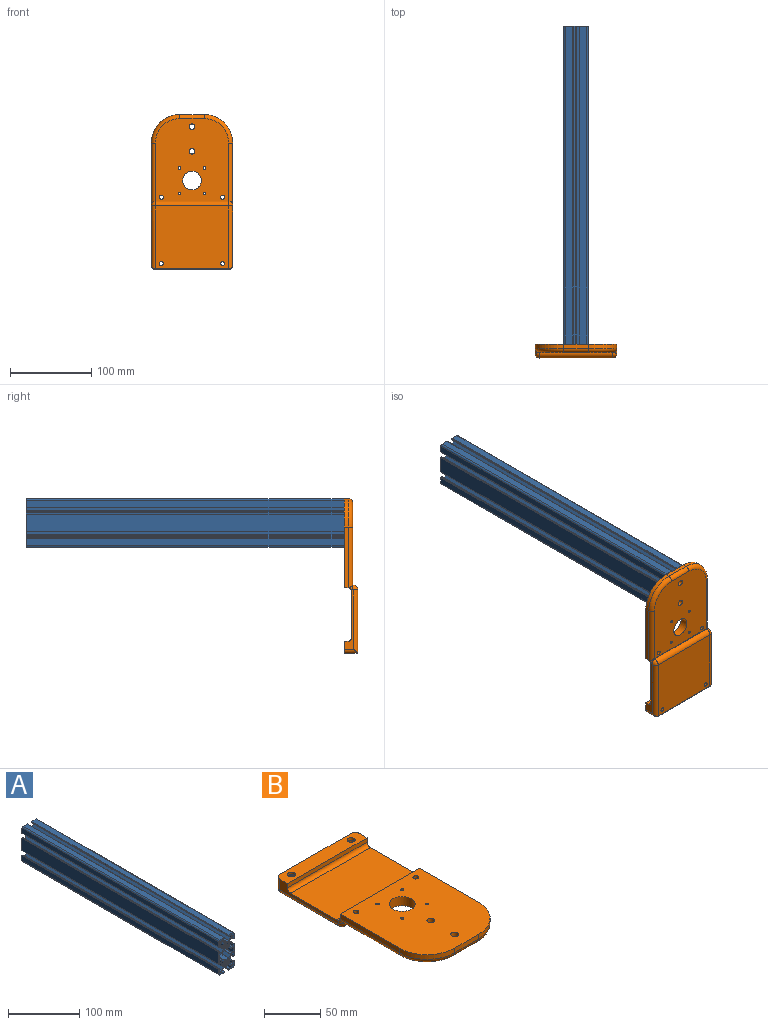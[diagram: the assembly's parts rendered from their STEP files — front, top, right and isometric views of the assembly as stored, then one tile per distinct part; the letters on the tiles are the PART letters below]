
ASSEMBLY  parts=2 mates=1
PART A: 312 faces, bbox 30x391x60 mm
  f0: cylinder r=0.4mm len=391mm, axis (0,1,0), area 245.7mm2, adj f1,f133,f310,f311
  f1: plane 391x8.6mm, normal (-1,0,0), area 3362.6mm2, adj f0,f2,f310,f311
  f2: cylinder r=2mm len=391mm, axis (0,1,0), area 1228.4mm2, adj f1,f3,f310,f311
  f3: plane 391x8.6mm, normal (0,0,-1), area 3362.6mm2, adj f2,f4,f310,f311
  f4: cylinder r=0.4mm len=391mm, axis (0,1,0), area 245.7mm2, adj f3,f5,f310,f311
  f5: plane 391x1.2mm, normal (1,0,0), area 469.2mm2, adj f4,f6,f310,f311
  f6: cylinder r=0.4mm len=391mm, axis (0,1,0), area 245.7mm2, adj f5,f7,f310,f311
  f7: plane 391x3.85mm, normal (0,0,1), area 1505.4mm2, adj f6,f8,f310,f311
  f8: plane 391x3.34mm, normal (1,0,0), area 1304.3mm2, adj f7,f9,f310,f311
  f9: plane 391x3.66mm, normal (0.71,0,-0.71), area 2026.2mm2, adj f8,f10,f310,f311
  f10: plane 391x3.93mm, normal (0,0,-1), area 1537.5mm2, adj f9,f11,f310,f311
  f11: cylinder r=0.5mm len=391mm, axis (0,1,0), area 102.4mm2, adj f10,f12,f310,f311
  f12: plane 391x0.4mm, normal (0.5,0,-0.87), area 182.2mm2, adj f11,f13,f310,f311
  f13: plane 391x0.4mm, normal (-0.5,0,-0.87), area 182.2mm2, adj f12,f14,f310,f311
  f14: cylinder r=0.5mm len=391mm, axis (0,1,0), area 204.7mm2, adj f13,f15,f310,f311
  f15: plane 391x0.32mm, normal (0.5,0,-0.87), area 142.4mm2, adj f14,f16,f310,f311
  f16: plane 391x1.28mm, normal (-0.19,0,-0.98), area 510.3mm2, adj f15,f17,f310,f311
  f17: plane 391x2.09mm, normal (0,0,-1), area 815.5mm2, adj f16,f18,f310,f311
  f18: plane 391x3.66mm, normal (-0.71,0,-0.71), area 2026.2mm2, adj f17,f19,f310,f311
  f19: plane 391x3.34mm, normal (-1,0,0), area 1304.3mm2, adj f18,f20,f310,f311
  f20: plane 391x3.85mm, normal (0,0,1), area 1505.4mm2, adj f19,f21,f310,f311
  f21: cylinder r=0.4mm len=391mm, axis (0,1,0), area 245.7mm2, adj f20,f22,f310,f311
  f22: plane 391x1.2mm, normal (-1,0,0), area 469.2mm2, adj f21,f23,f310,f311
  f23: cylinder r=0.4mm len=391mm, axis (0,1,0), area 245.7mm2, adj f22,f24,f310,f311
  f24: plane 391x8.6mm, normal (0,0,-1), area 3362.6mm2, adj f23,f25,f310,f311
  f25: cylinder r=2mm len=391mm, axis (0,1,0), area 1228.4mm2, adj f24,f26,f310,f311
  f26: plane 391x8.6mm, normal (1,0,0), area 3362.6mm2, adj f25,f27,f310,f311
  f27: cylinder r=0.4mm len=391mm, axis (0,1,0), area 245.7mm2, adj f26,f28,f310,f311
  f28: plane 391x1.2mm, normal (0,0,1), area 469.2mm2, adj f27,f29,f310,f311
  f29: cylinder r=0.4mm len=391mm, axis (0,1,0), area 245.7mm2, adj f28,f30,f310,f311
  f30: plane 391x3.85mm, normal (-1,0,0), area 1505.3mm2, adj f29,f31,f310,f311
  f31: plane 391x3.34mm, normal (0,0,1), area 1304.3mm2, adj f30,f32,f310,f311
  f32: plane 391x3.66mm, normal (0.71,0,0.71), area 2026.2mm2, adj f31,f33,f310,f311
  f33: plane 391x3.93mm, normal (1,0,0), area 1537.5mm2, adj f32,f34,f310,f311
  f34: cylinder r=0.5mm len=391mm, axis (0,1,0), area 102.4mm2, adj f33,f35,f310,f311
  f35: plane 391x0.4mm, normal (0.87,0,0.5), area 182.2mm2, adj f34,f36,f310,f311
  f36: plane 391x0.4mm, normal (0.87,0,-0.5), area 182.2mm2, adj f35,f37,f310,f311
  f37: cylinder r=0.5mm len=391mm, axis (0,1,0), area 204.7mm2, adj f36,f38,f310,f311
  f38: plane 391x0.32mm, normal (0.87,0,0.5), area 142.4mm2, adj f37,f39,f310,f311
  f39: plane 391x1.28mm, normal (0.98,0,-0.19), area 510.3mm2, adj f38,f40,f310,f311
  f40: plane 391x2.09mm, normal (1,0,0), area 815.5mm2, adj f39,f41,f310,f311
  f41: plane 391x3.66mm, normal (0.71,0,-0.71), area 2026.2mm2, adj f40,f42,f310,f311
  f42: plane 391x3.34mm, normal (0,0,-1), area 1304.3mm2, adj f41,f43,f310,f311
  f43: plane 391x3.85mm, normal (-1,0,0), area 1505.4mm2, adj f42,f44,f310,f311
  f44: cylinder r=0.4mm len=391mm, axis (0,1,0), area 245.7mm2, adj f43,f45,f310,f311
  f45: plane 391x1.2mm, normal (0,0,-1), area 469.2mm2, adj f44,f46,f310,f311
  f46: cylinder r=0.4mm len=391mm, axis (0,1,0), area 245.7mm2, adj f45,f47,f310,f311
  f47: plane 391x21.2mm, normal (1,0,0), area 8289.2mm2, adj f46,f48,f310,f311
  f48: cylinder r=0.4mm len=391mm, axis (0,1,0), area 245.7mm2, adj f47,f49,f310,f311
  f49: plane 391x1.2mm, normal (0,0,1), area 469.2mm2, adj f48,f50,f310,f311
  f50: cylinder r=0.4mm len=391mm, axis (0,1,0), area 245.7mm2, adj f49,f51,f310,f311
  f51: plane 391x3.85mm, normal (-1,0,0), area 1505.4mm2, adj f50,f52,f310,f311
  f52: plane 391x3.34mm, normal (0,0,1), area 1304.3mm2, adj f51,f53,f310,f311
  f53: plane 391x3.66mm, normal (0.71,0,0.71), area 2026.2mm2, adj f52,f54,f310,f311
  f54: plane 391x3.93mm, normal (1,0,0), area 1537.5mm2, adj f53,f55,f310,f311
  f55: cylinder r=0.5mm len=391mm, axis (0,1,0), area 102.4mm2, adj f54,f56,f310,f311
  f56: plane 391x0.4mm, normal (0.87,0,0.5), area 182.2mm2, adj f55,f57,f310,f311
  f57: plane 391x0.4mm, normal (0.87,0,-0.5), area 182.2mm2, adj f56,f58,f310,f311
  f58: cylinder r=0.5mm len=391mm, axis (0,1,0), area 204.7mm2, adj f57,f59,f310,f311
  f59: plane 391x0.32mm, normal (0.87,0,0.5), area 142.4mm2, adj f58,f60,f310,f311
  f60: plane 391x1.28mm, normal (0.98,0,-0.19), area 510.3mm2, adj f59,f61,f310,f311
  f61: plane 391x2.09mm, normal (1,0,0), area 815.5mm2, adj f60,f62,f310,f311
  f62: plane 391x3.66mm, normal (0.71,0,-0.71), area 2026.2mm2, adj f61,f63,f310,f311
  f63: plane 391x3.34mm, normal (0,0,-1), area 1304.3mm2, adj f62,f64,f310,f311
  f64: plane 391x3.85mm, normal (-1,0,0), area 1505.3mm2, adj f63,f65,f310,f311
  f65: cylinder r=0.4mm len=391mm, axis (0,1,0), area 245.7mm2, adj f64,f66,f310,f311
  f66: plane 391x1.2mm, normal (0,0,-1), area 469.2mm2, adj f65,f67,f310,f311
  f67: cylinder r=0.4mm len=391mm, axis (0,1,0), area 245.7mm2, adj f66,f68,f310,f311
  f68: plane 391x8.6mm, normal (1,0,0), area 3362.6mm2, adj f67,f69,f310,f311
  f69: cylinder r=2mm len=391mm, axis (0,1,0), area 1228.4mm2, adj f68,f70,f310,f311
  f70: plane 391x8.6mm, normal (0,0,1), area 3362.6mm2, adj f69,f71,f310,f311
  f71: cylinder r=0.4mm len=391mm, axis (0,1,0), area 245.7mm2, adj f70,f72,f310,f311
  f72: plane 391x1.2mm, normal (-1,0,0), area 469.2mm2, adj f71,f73,f310,f311
  f73: cylinder r=0.4mm len=391mm, axis (0,1,0), area 245.7mm2, adj f72,f74,f310,f311
  f74: plane 391x3.85mm, normal (0,0,-1), area 1505.4mm2, adj f73,f75,f310,f311
  f75: plane 391x3.34mm, normal (-1,0,0), area 1304.3mm2, adj f74,f76,f310,f311
  f76: plane 391x3.66mm, normal (-0.71,0,0.71), area 2026.2mm2, adj f75,f77,f310,f311
  f77: plane 391x3.93mm, normal (0,0,1), area 1537.5mm2, adj f76,f78,f310,f311
  f78: cylinder r=0.5mm len=391mm, axis (0,1,0), area 102.4mm2, adj f77,f79,f310,f311
  f79: plane 391x0.4mm, normal (-0.5,0,0.87), area 182.2mm2, adj f78,f80,f310,f311
  f80: plane 391x0.4mm, normal (0.5,0,0.87), area 182.2mm2, adj f79,f81,f310,f311
  f81: cylinder r=0.5mm len=391mm, axis (0,1,0), area 204.7mm2, adj f80,f82,f310,f311
  f82: plane 391x0.32mm, normal (-0.5,0,0.87), area 142.4mm2, adj f81,f83,f310,f311
  f83: plane 391x1.28mm, normal (0.19,0,0.98), area 510.3mm2, adj f82,f84,f310,f311
  f84: plane 391x2.09mm, normal (0,0,1), area 815.5mm2, adj f83,f85,f310,f311
  f85: plane 391x3.66mm, normal (0.71,0,0.71), area 2026.2mm2, adj f84,f86,f310,f311
  f86: plane 391x3.34mm, normal (1,0,0), area 1304.3mm2, adj f85,f87,f310,f311
  f87: plane 391x3.85mm, normal (0,0,-1), area 1505.4mm2, adj f86,f88,f310,f311
  f88: cylinder r=0.4mm len=391mm, axis (0,1,0), area 245.7mm2, adj f87,f89,f310,f311
  f89: plane 391x1.2mm, normal (1,0,0), area 469.2mm2, adj f88,f90,f310,f311
  f90: cylinder r=0.4mm len=391mm, axis (0,1,0), area 245.7mm2, adj f89,f91,f310,f311
  f91: plane 391x8.6mm, normal (0,0,1), area 3362.6mm2, adj f90,f92,f310,f311
  f92: cylinder r=2mm len=391mm, axis (0,1,0), area 1228.4mm2, adj f91,f93,f310,f311
  f93: plane 391x8.6mm, normal (-1,0,0), area 3362.6mm2, adj f92,f94,f310,f311
  f94: cylinder r=0.4mm len=391mm, axis (0,1,0), area 245.7mm2, adj f93,f95,f310,f311
  f95: plane 391x1.2mm, normal (0,0,-1), area 469.2mm2, adj f94,f96,f310,f311
  f96: cylinder r=0.4mm len=391mm, axis (0,1,0), area 245.7mm2, adj f95,f97,f310,f311
  f97: plane 391x3.85mm, normal (1,0,0), area 1505.3mm2, adj f96,f98,f310,f311
  f98: plane 391x3.34mm, normal (0,0,-1), area 1304.3mm2, adj f97,f99,f310,f311
  f99: plane 391x3.66mm, normal (-0.71,0,-0.71), area 2026.2mm2, adj f98,f100,f310,f311
  f100: plane 391x3.93mm, normal (-1,0,0), area 1537.5mm2, adj f99,f101,f310,f311
  f101: cylinder r=0.5mm len=391mm, axis (0,1,0), area 102.4mm2, adj f100,f102,f310,f311
  f102: plane 391x0.4mm, normal (-0.87,0,-0.5), area 182.2mm2, adj f101,f103,f310,f311
  f103: plane 391x0.4mm, normal (-0.87,0,0.5), area 182.2mm2, adj f102,f104,f310,f311
  f104: cylinder r=0.5mm len=391mm, axis (0,1,0), area 204.7mm2, adj f103,f105,f310,f311
  f105: plane 391x0.32mm, normal (-0.87,0,-0.5), area 142.4mm2, adj f104,f106,f310,f311
  f106: plane 391x1.28mm, normal (-0.98,0,0.19), area 510.3mm2, adj f105,f107,f310,f311
  f107: plane 391x2.09mm, normal (-1,0,0), area 815.5mm2, adj f106,f108,f310,f311
  f108: plane 391x3.66mm, normal (-0.71,0,0.71), area 2026.2mm2, adj f107,f109,f310,f311
  f109: plane 391x3.34mm, normal (0,0,1), area 1304.3mm2, adj f108,f110,f310,f311
  f110: plane 391x3.85mm, normal (1,0,0), area 1505.4mm2, adj f109,f111,f310,f311
  f111: cylinder r=0.4mm len=391mm, axis (0,1,0), area 245.7mm2, adj f110,f112,f310,f311
  f112: plane 391x1.2mm, normal (0,0,1), area 469.2mm2, adj f111,f113,f310,f311
  f113: cylinder r=0.4mm len=391mm, axis (0,1,0), area 245.7mm2, adj f112,f114,f310,f311
  f114: plane 391x21.2mm, normal (-1,0,0), area 8289.2mm2, adj f113,f115,f310,f311
  f115: cylinder r=0.4mm len=391mm, axis (0,1,0), area 245.7mm2, adj f114,f116,f310,f311
  f116: plane 391x1.2mm, normal (0,0,-1), area 469.2mm2, adj f115,f117,f310,f311
  f117: cylinder r=0.4mm len=391mm, axis (0,1,0), area 245.7mm2, adj f116,f118,f310,f311
  f118: plane 391x3.85mm, normal (1,0,0), area 1505.4mm2, adj f117,f119,f310,f311
  f119: plane 391x3.34mm, normal (0,0,-1), area 1304.3mm2, adj f118,f120,f310,f311
  f120: plane 391x3.66mm, normal (-0.71,0,-0.71), area 2026.2mm2, adj f119,f121,f310,f311
  f121: plane 391x3.93mm, normal (-1,0,0), area 1537.5mm2, adj f120,f122,f310,f311
  f122: cylinder r=0.5mm len=391mm, axis (0,1,0), area 102.4mm2, adj f121,f123,f310,f311
  f123: plane 391x0.4mm, normal (-0.87,0,-0.5), area 182.2mm2, adj f122,f124,f310,f311
  f124: plane 391x0.4mm, normal (-0.87,0,0.5), area 182.2mm2, adj f123,f125,f310,f311
  f125: cylinder r=0.5mm len=391mm, axis (0,1,0), area 204.7mm2, adj f124,f126,f310,f311
  f126: plane 391x0.32mm, normal (-0.87,0,-0.5), area 142.4mm2, adj f125,f127,f310,f311
  f127: plane 391x1.28mm, normal (-0.98,0,0.19), area 510.3mm2, adj f126,f128,f310,f311
  f128: plane 391x2.09mm, normal (-1,0,0), area 815.5mm2, adj f127,f129,f310,f311
  f129: plane 391x3.66mm, normal (-0.71,0,0.71), area 2026.2mm2, adj f128,f130,f310,f311
  f130: plane 391x3.34mm, normal (0,0,1), area 1304.3mm2, adj f129,f131,f310,f311
  f131: plane 391x3.85mm, normal (1,0,0), area 1505.3mm2, adj f130,f132,f310,f311
  f132: cylinder r=0.4mm len=391mm, axis (0,1,0), area 245.7mm2, adj f131,f133,f310,f311
  f133: plane 391x1.2mm, normal (0,0,1), area 469.2mm2, adj f0,f132,f310,f311
  f134: plane 391x0.25mm, normal (0,0,-1), area 98.2mm2, adj f135,f137,f310,f311
  f135: cylinder r=0.5mm len=391mm, axis (0,1,0), area 184.9mm2, adj f134,f143,f310,f311
  f136: plane 391x2.05mm, normal (1,0,0), area 801.5mm2, adj f137,f138,f310,f311
  f137: cylinder r=0.5mm len=391mm, axis (0,1,0), area 307.1mm2, adj f134,f136,f310,f311
  f138: cylinder r=0.5mm len=391mm, axis (0,1,0), area 307.1mm2, adj f136,f139,f310,f311
  f139: plane 391x2.75mm, normal (0,0,1), area 1075.2mm2, adj f138,f140,f310,f311
  f140: cylinder r=0.5mm len=391mm, axis (0,1,0), area 307.1mm2, adj f139,f141,f310,f311
  f141: plane 391x0.17mm, normal (-1,0,0), area 64.5mm2, adj f140,f142,f310,f311
  f142: cylinder r=0.5mm len=391mm, axis (0,1,0), area 239.3mm2, adj f141,f143,f310,f311
  f143: cylinder r=4.8mm len=391mm, axis (0,1,0), area 1125.2mm2, adj f135,f142,f310,f311
  f144: cylinder r=0.5mm len=391mm, axis (0,1,0), area 307.1mm2, adj f145,f153,f310,f311
  f145: plane 391x0.25mm, normal (0,0,1), area 98.2mm2, adj f144,f146,f310,f311
  f146: cylinder r=0.5mm len=391mm, axis (0,1,0), area 184.9mm2, adj f145,f147,f310,f311
  f147: cylinder r=4.8mm len=391mm, axis (0,1,0), area 1125.2mm2, adj f146,f148,f310,f311
  f148: cylinder r=0.5mm len=391mm, axis (0,1,0), area 239.3mm2, adj f147,f149,f310,f311
  f149: plane 391x0.17mm, normal (-1,0,0), area 64.5mm2, adj f148,f150,f310,f311
  f150: cylinder r=0.5mm len=391mm, axis (0,1,0), area 307.1mm2, adj f149,f151,f310,f311
  f151: plane 391x2.75mm, normal (0,0,-1), area 1075.2mm2, adj f150,f152,f310,f311
  f152: cylinder r=0.5mm len=391mm, axis (0,1,0), area 307.1mm2, adj f151,f153,f310,f311
  f153: plane 391x2.05mm, normal (1,0,0), area 801.5mm2, adj f144,f152,f310,f311
  f154: plane 391x0.17mm, normal (1,0,0), area 64.5mm2, adj f155,f163,f310,f311
  f155: cylinder r=0.5mm len=391mm, axis (0,1,0), area 239.3mm2, adj f154,f156,f310,f311
  f156: cylinder r=4.8mm len=391mm, axis (0,1,0), area 1125.2mm2, adj f155,f157,f310,f311
  f157: cylinder r=0.5mm len=391mm, axis (0,1,0), area 184.9mm2, adj f156,f158,f310,f311
  f158: plane 391x0.25mm, normal (0,0,-1), area 98.2mm2, adj f157,f159,f310,f311
  f159: cylinder r=0.5mm len=391mm, axis (0,1,0), area 307.1mm2, adj f158,f160,f310,f311
  f160: plane 391x2.05mm, normal (-1,0,0), area 801.5mm2, adj f159,f161,f310,f311
  f161: cylinder r=0.5mm len=391mm, axis (0,1,0), area 307.1mm2, adj f160,f162,f310,f311
  f162: plane 391x2.75mm, normal (0,0,1), area 1075.2mm2, adj f161,f163,f310,f311
  f163: cylinder r=0.5mm len=391mm, axis (0,1,0), area 307.1mm2, adj f154,f162,f310,f311
  f164: cylinder r=0.5mm len=391mm, axis (0,1,0), area 239.3mm2, adj f165,f173,f310,f311
  f165: cylinder r=4.8mm len=391mm, axis (0,1,0), area 1125.2mm2, adj f164,f166,f310,f311
  f166: cylinder r=0.5mm len=391mm, axis (0,1,0), area 184.9mm2, adj f165,f167,f310,f311
  f167: plane 391x0.25mm, normal (0,0,1), area 98.2mm2, adj f166,f168,f310,f311
  f168: cylinder r=0.5mm len=391mm, axis (0,1,0), area 307.1mm2, adj f167,f169,f310,f311
  f169: plane 391x2.05mm, normal (-1,0,0), area 801.5mm2, adj f168,f170,f310,f311
  f170: cylinder r=0.5mm len=391mm, axis (0,1,0), area 307.1mm2, adj f169,f171,f310,f311
  f171: plane 391x2.75mm, normal (0,0,-1), area 1075.2mm2, adj f170,f172,f310,f311
  f172: cylinder r=0.5mm len=391mm, axis (0,1,0), area 307.1mm2, adj f171,f173,f310,f311
  f173: plane 391x0.17mm, normal (1,0,0), area 64.5mm2, adj f164,f172,f310,f311
  f174: cylinder r=1mm len=391mm, axis (0,1,0), area 614.2mm2, adj f175,f197,f310,f311
  f175: plane 391x3.15mm, normal (0,0,1), area 1231.7mm2, adj f174,f176,f310,f311
  f176: cylinder r=1mm len=391mm, axis (0,1,0), area 307.1mm2, adj f175,f177,f310,f311
  f177: plane 391x3.86mm, normal (0.71,0,0.71), area 2136.7mm2, adj f176,f178,f310,f311
  f178: cylinder r=1mm len=391mm, axis (0,1,0), area 307.1mm2, adj f177,f179,f310,f311
  f179: plane 391x7.94mm, normal (0,0,1), area 3105.8mm2, adj f178,f180,f310,f311
  f180: cylinder r=1mm len=391mm, axis (0,1,0), area 307.1mm2, adj f179,f181,f310,f311
  f181: plane 391x3.86mm, normal (-0.71,0,0.71), area 2136.7mm2, adj f180,f182,f310,f311
  f182: cylinder r=1mm len=391mm, axis (0,1,0), area 307.1mm2, adj f181,f183,f310,f311
  f183: plane 391x3.15mm, normal (0,0,1), area 1231.7mm2, adj f182,f184,f310,f311
  f184: cylinder r=1mm len=391mm, axis (0,1,0), area 614.2mm2, adj f183,f185,f310,f311
  f185: plane 391x7.5mm, normal (-1,0,0), area 2932.5mm2, adj f184,f186,f310,f311
  f186: cylinder r=1mm len=391mm, axis (0,1,0), area 614.2mm2, adj f185,f187,f310,f311
  f187: plane 391x3.15mm, normal (0,0,-1), area 1231.7mm2, adj f186,f188,f310,f311
  f188: cylinder r=1mm len=391mm, axis (0,1,0), area 307.1mm2, adj f187,f189,f310,f311
  f189: plane 391x3.86mm, normal (-0.71,0,-0.71), area 2136.7mm2, adj f188,f190,f310,f311
  f190: cylinder r=1mm len=391mm, axis (0,1,0), area 307.1mm2, adj f189,f191,f310,f311
  f191: plane 391x7.94mm, normal (0,0,-1), area 3105.8mm2, adj f190,f192,f310,f311
  f192: cylinder r=1mm len=391mm, axis (0,1,0), area 307.1mm2, adj f191,f193,f310,f311
  f193: plane 391x3.86mm, normal (0.71,0,-0.71), area 2136.7mm2, adj f192,f194,f310,f311
  f194: cylinder r=1mm len=391mm, axis (0,1,0), area 307.1mm2, adj f193,f195,f310,f311
  f195: plane 391x3.15mm, normal (0,0,-1), area 1231.7mm2, adj f194,f196,f310,f311
  f196: cylinder r=1mm len=391mm, axis (0,1,0), area 614.2mm2, adj f195,f197,f310,f311
  f197: plane 391x7.5mm, normal (1,0,0), area 2932.5mm2, adj f174,f196,f310,f311
  f198: plane 391x1.74mm, normal (1,0,0), area 679.5mm2, adj f199,f253,f310,f311
  f199: cylinder r=0.4mm len=391mm, axis (0,1,0), area 30mm2, adj f198,f200,f310,f311
  f200: plane 391x0.76mm, normal (0.98,0,-0.19), area 303.6mm2, adj f199,f201,f310,f311
  f201: cylinder r=0.4mm len=391mm, axis (0,1,0), area 215.6mm2, adj f200,f202,f310,f311
  f202: plane 391x0.61mm, normal (0,0,-1), area 240.3mm2, adj f201,f203,f310,f311
  f203: cylinder r=0.4mm len=391mm, axis (0,1,0), area 291.6mm2, adj f202,f204,f310,f311
  f204: cylinder r=3.4mm len=391mm, axis (0,1,0), area 780.8mm2, adj f203,f205,f310,f311
  f205: cylinder r=0.4mm len=391mm, axis (0,1,0), area 291.6mm2, adj f204,f206,f310,f311
  f206: plane 391x0.61mm, normal (0,0,1), area 240.3mm2, adj f205,f207,f310,f311
  f207: cylinder r=0.4mm len=391mm, axis (0,1,0), area 215.6mm2, adj f206,f208,f310,f311
  f208: plane 391x0.76mm, normal (0.98,0,0.19), area 303.6mm2, adj f207,f209,f310,f311
  f209: cylinder r=0.4mm len=391mm, axis (0,1,0), area 30mm2, adj f208,f210,f310,f311
  f210: plane 391x1.74mm, normal (1,0,0), area 679.5mm2, adj f209,f211,f310,f311
  f211: cylinder r=0.4mm len=391mm, axis (0,1,0), area 245.7mm2, adj f210,f212,f310,f311
  f212: plane 391x1.74mm, normal (0,0,-1), area 679.5mm2, adj f211,f213,f310,f311
  f213: cylinder r=0.4mm len=391mm, axis (0,1,0), area 30mm2, adj f212,f214,f310,f311
  f214: plane 391x0.76mm, normal (-0.19,0,-0.98), area 303.6mm2, adj f213,f215,f310,f311
  f215: cylinder r=0.4mm len=391mm, axis (0,1,0), area 215.6mm2, adj f214,f216,f310,f311
  f216: plane 391x0.61mm, normal (-1,0,0), area 240.3mm2, adj f215,f217,f310,f311
  f217: cylinder r=0.4mm len=391mm, axis (0,1,0), area 291.6mm2, adj f216,f218,f310,f311
  f218: cylinder r=3.4mm len=391mm, axis (0,1,0), area 780.8mm2, adj f217,f219,f310,f311
  f219: cylinder r=0.4mm len=391mm, axis (0,1,0), area 291.6mm2, adj f218,f220,f310,f311
  f220: plane 391x0.61mm, normal (1,0,0), area 240.3mm2, adj f219,f221,f310,f311
  f221: cylinder r=0.4mm len=391mm, axis (0,1,0), area 215.6mm2, adj f220,f222,f310,f311
  f222: plane 391x0.76mm, normal (0.19,0,-0.98), area 303.6mm2, adj f221,f223,f310,f311
  f223: cylinder r=0.4mm len=391mm, axis (0,1,0), area 30mm2, adj f222,f224,f310,f311
  f224: plane 391x1.74mm, normal (0,0,-1), area 679.5mm2, adj f223,f225,f310,f311
  f225: cylinder r=0.4mm len=391mm, axis (0,1,0), area 245.7mm2, adj f224,f226,f310,f311
  f226: plane 391x1.74mm, normal (-1,0,0), area 679.5mm2, adj f225,f227,f310,f311
  f227: cylinder r=0.4mm len=391mm, axis (0,1,0), area 30mm2, adj f226,f228,f310,f311
  f228: plane 391x0.76mm, normal (-0.98,0,0.19), area 303.6mm2, adj f227,f229,f310,f311
  f229: cylinder r=0.4mm len=391mm, axis (0,1,0), area 215.6mm2, adj f228,f230,f310,f311
  f230: plane 391x0.61mm, normal (0,0,1), area 240.3mm2, adj f229,f231,f310,f311
  f231: cylinder r=0.4mm len=391mm, axis (0,1,0), area 291.6mm2, adj f230,f232,f310,f311
  f232: cylinder r=3.4mm len=391mm, axis (0,1,0), area 780.8mm2, adj f231,f233,f310,f311
  f233: cylinder r=0.4mm len=391mm, axis (0,1,0), area 291.6mm2, adj f232,f234,f310,f311
  f234: plane 391x0.61mm, normal (0,0,-1), area 240.3mm2, adj f233,f235,f310,f311
  f235: cylinder r=0.4mm len=391mm, axis (0,1,0), area 215.6mm2, adj f234,f236,f310,f311
  f236: plane 391x0.76mm, normal (-0.98,0,-0.19), area 303.6mm2, adj f235,f237,f310,f311
  f237: cylinder r=0.4mm len=391mm, axis (0,1,0), area 30mm2, adj f236,f238,f310,f311
  f238: plane 391x1.74mm, normal (-1,0,0), area 679.5mm2, adj f237,f239,f310,f311
  f239: cylinder r=0.4mm len=391mm, axis (0,1,0), area 245.7mm2, adj f238,f240,f310,f311
  f240: plane 391x1.74mm, normal (0,0,1), area 679.5mm2, adj f239,f241,f310,f311
  f241: cylinder r=0.4mm len=391mm, axis (0,1,0), area 30mm2, adj f240,f242,f310,f311
  f242: plane 391x0.76mm, normal (0.19,0,0.98), area 303.6mm2, adj f241,f243,f310,f311
  f243: cylinder r=0.4mm len=391mm, axis (0,1,0), area 215.6mm2, adj f242,f244,f310,f311
  f244: plane 391x0.61mm, normal (1,0,0), area 240.3mm2, adj f243,f245,f310,f311
  f245: cylinder r=0.4mm len=391mm, axis (0,1,0), area 291.6mm2, adj f244,f246,f310,f311
  f246: cylinder r=3.4mm len=391mm, axis (0,1,0), area 780.8mm2, adj f245,f247,f310,f311
  f247: cylinder r=0.4mm len=391mm, axis (0,1,0), area 291.6mm2, adj f246,f248,f310,f311
  f248: plane 391x0.61mm, normal (-1,0,0), area 240.3mm2, adj f247,f249,f310,f311
  f249: cylinder r=0.4mm len=391mm, axis (0,1,0), area 215.6mm2, adj f248,f250,f310,f311
  f250: plane 391x0.76mm, normal (-0.19,0,0.98), area 303.6mm2, adj f249,f251,f310,f311
  f251: cylinder r=0.4mm len=391mm, axis (0,1,0), area 30mm2, adj f250,f252,f310,f311
  f252: plane 391x1.74mm, normal (0,0,1), area 679.5mm2, adj f251,f253,f310,f311
  f253: cylinder r=0.4mm len=391mm, axis (0,1,0), area 245.7mm2, adj f198,f252,f310,f311
  f254: cylinder r=0.4mm len=391mm, axis (0,1,0), area 245.7mm2, adj f255,f309,f310,f311
  f255: plane 391x1.74mm, normal (0,0,1), area 679.5mm2, adj f254,f256,f310,f311
  f256: cylinder r=0.4mm len=391mm, axis (0,1,0), area 30mm2, adj f255,f257,f310,f311
  f257: plane 391x0.76mm, normal (-0.19,0,0.98), area 303.6mm2, adj f256,f258,f310,f311
  f258: cylinder r=0.4mm len=391mm, axis (0,1,0), area 215.6mm2, adj f257,f259,f310,f311
  f259: plane 391x0.61mm, normal (-1,0,0), area 240.3mm2, adj f258,f260,f310,f311
  f260: cylinder r=0.4mm len=391mm, axis (0,1,0), area 291.6mm2, adj f259,f261,f310,f311
  f261: cylinder r=3.4mm len=391mm, axis (0,1,0), area 780.8mm2, adj f260,f262,f310,f311
  f262: cylinder r=0.4mm len=391mm, axis (0,1,0), area 291.6mm2, adj f261,f263,f310,f311
  f263: plane 391x0.61mm, normal (1,0,0), area 240.3mm2, adj f262,f264,f310,f311
  f264: cylinder r=0.4mm len=391mm, axis (0,1,0), area 215.6mm2, adj f263,f265,f310,f311
  f265: plane 391x0.76mm, normal (0.19,0,0.98), area 303.6mm2, adj f264,f266,f310,f311
  f266: cylinder r=0.4mm len=391mm, axis (0,1,0), area 30mm2, adj f265,f267,f310,f311
  f267: plane 391x1.74mm, normal (0,0,1), area 679.5mm2, adj f266,f268,f310,f311
  f268: cylinder r=0.4mm len=391mm, axis (0,1,0), area 245.7mm2, adj f267,f269,f310,f311
  f269: plane 391x1.74mm, normal (-1,0,0), area 679.5mm2, adj f268,f270,f310,f311
  f270: cylinder r=0.4mm len=391mm, axis (0,1,0), area 30mm2, adj f269,f271,f310,f311
  f271: plane 391x0.76mm, normal (-0.98,0,-0.19), area 303.6mm2, adj f270,f272,f310,f311
  f272: cylinder r=0.4mm len=391mm, axis (0,1,0), area 215.6mm2, adj f271,f273,f310,f311
  f273: plane 391x0.61mm, normal (0,0,-1), area 240.3mm2, adj f272,f274,f310,f311
  f274: cylinder r=0.4mm len=391mm, axis (0,1,0), area 291.6mm2, adj f273,f275,f310,f311
  f275: cylinder r=3.4mm len=391mm, axis (0,1,0), area 780.8mm2, adj f274,f276,f310,f311
  f276: cylinder r=0.4mm len=391mm, axis (0,1,0), area 291.6mm2, adj f275,f277,f310,f311
  f277: plane 391x0.61mm, normal (0,0,1), area 240.3mm2, adj f276,f278,f310,f311
  f278: cylinder r=0.4mm len=391mm, axis (0,1,0), area 215.6mm2, adj f277,f279,f310,f311
  f279: plane 391x0.76mm, normal (-0.98,0,0.19), area 303.6mm2, adj f278,f280,f310,f311
  f280: cylinder r=0.4mm len=391mm, axis (0,1,0), area 30mm2, adj f279,f281,f310,f311
  f281: plane 391x1.74mm, normal (-1,0,0), area 679.5mm2, adj f280,f282,f310,f311
  f282: cylinder r=0.4mm len=391mm, axis (0,1,0), area 245.7mm2, adj f281,f283,f310,f311
  f283: plane 391x1.74mm, normal (0,0,-1), area 679.5mm2, adj f282,f284,f310,f311
  f284: cylinder r=0.4mm len=391mm, axis (0,1,0), area 30mm2, adj f283,f285,f310,f311
  f285: plane 391x0.76mm, normal (0.19,0,-0.98), area 303.6mm2, adj f284,f286,f310,f311
  f286: cylinder r=0.4mm len=391mm, axis (0,1,0), area 215.6mm2, adj f285,f287,f310,f311
  f287: plane 391x0.61mm, normal (1,0,0), area 240.3mm2, adj f286,f288,f310,f311
  f288: cylinder r=0.4mm len=391mm, axis (0,1,0), area 291.6mm2, adj f287,f289,f310,f311
  f289: cylinder r=3.4mm len=391mm, axis (0,1,0), area 780.8mm2, adj f288,f290,f310,f311
  f290: cylinder r=0.4mm len=391mm, axis (0,1,0), area 291.6mm2, adj f289,f291,f310,f311
  f291: plane 391x0.61mm, normal (-1,0,0), area 240.3mm2, adj f290,f292,f310,f311
  f292: cylinder r=0.4mm len=391mm, axis (0,1,0), area 215.6mm2, adj f291,f293,f310,f311
  f293: plane 391x0.76mm, normal (-0.19,0,-0.98), area 303.6mm2, adj f292,f294,f310,f311
  f294: cylinder r=0.4mm len=391mm, axis (0,1,0), area 30mm2, adj f293,f295,f310,f311
  f295: plane 391x1.74mm, normal (0,0,-1), area 679.5mm2, adj f294,f296,f310,f311
  f296: cylinder r=0.4mm len=391mm, axis (0,1,0), area 245.7mm2, adj f295,f297,f310,f311
  f297: plane 391x1.74mm, normal (1,0,0), area 679.5mm2, adj f296,f298,f310,f311
  f298: cylinder r=0.4mm len=391mm, axis (0,1,0), area 30mm2, adj f297,f299,f310,f311
  f299: plane 391x0.76mm, normal (0.98,0,0.19), area 303.6mm2, adj f298,f300,f310,f311
  f300: cylinder r=0.4mm len=391mm, axis (0,1,0), area 215.6mm2, adj f299,f301,f310,f311
  f301: plane 391x0.61mm, normal (0,0,1), area 240.3mm2, adj f300,f302,f310,f311
  f302: cylinder r=0.4mm len=391mm, axis (0,1,0), area 291.6mm2, adj f301,f303,f310,f311
  f303: cylinder r=3.4mm len=391mm, axis (0,1,0), area 780.8mm2, adj f302,f304,f310,f311
  f304: cylinder r=0.4mm len=391mm, axis (0,1,0), area 291.6mm2, adj f303,f305,f310,f311
  f305: plane 391x0.61mm, normal (0,0,-1), area 240.3mm2, adj f304,f306,f310,f311
  f306: cylinder r=0.4mm len=391mm, axis (0,1,0), area 215.6mm2, adj f305,f307,f310,f311
  f307: plane 391x0.76mm, normal (0.98,0,-0.19), area 303.6mm2, adj f306,f308,f310,f311
  f308: cylinder r=0.4mm len=391mm, axis (0,1,0), area 30mm2, adj f307,f309,f310,f311
  f309: plane 391x1.74mm, normal (1,0,0), area 679.5mm2, adj f254,f308,f310,f311
  f310: plane 60x30mm, normal (0,-1,0), area 536mm2, adj f0,f1,f2,f3,f4,f5,f6,f7
  f311: plane 60x30mm, normal (0,1,0), area 536mm2, adj f0,f1,f2,f3,f4,f5,f6,f7
PART B: 50 faces, bbox 105.8x193.2x16.5 mm
  f0: cylinder r=2.5mm len=13.8mm, axis (0,0,1), area 216.8mm2, adj f4,f49
  f1: cylinder r=2.5mm len=13.8mm, axis (0,0,1), area 216.8mm2, adj f4,f46
  f2: plane 74.33x5mm, normal (1,0,0), area 371.5mm2, adj f15,f24,f25,f30,f38
  f3: plane 74.33x5mm, normal (-1,0,0), area 371.5mm2, adj f15,f24,f25,f29,f45
  f4: plane 90x77mm, normal (0,0,-1), area 6890.7mm2, adj f0,f1,f18,f19,f33,f39
  f5: plane 100x15mm, normal (0,0,1), area 1409.9mm2, adj f6,f8,f20,f21,f31,f35,f47,f48
  f6: plane 74x11.5mm, normal (-1,0,0), area 310.6mm2, adj f5,f21,f22,f23,f24,f35,f39,f41
  f7: plane 30x5mm, normal (0,-1,0), area 150mm2, adj f15,f29,f30,f42
  f8: plane 74x11.5mm, normal (1,0,0), area 310.6mm2, adj f5,f21,f22,f23,f24,f31,f33,f34
  f9: cylinder r=1.5mm len=10mm, axis (0,0,-1), area 94.2mm2, adj f15,f16
  f10: cylinder r=1.5mm len=10mm, axis (0,0,-1), area 94.2mm2, adj f15,f16
  f11: cylinder r=1.5mm len=10mm, axis (0,0,-1), area 94.2mm2, adj f15,f16
  f12: cylinder r=1.5mm len=10mm, axis (0,0,-1), area 94.2mm2, adj f15,f16
  f13: cylinder r=11.5mm len=23mm, axis (0,0,-1), area 722.6mm2, adj f15,f16
  f14: cylinder r=2.5mm len=10mm, axis (0,0,-1), area 157.1mm2, adj f15,f16
  f15: plane 109.3x100mm, normal (0,0,1), area 9844.2mm2, adj f2,f3,f7,f9,f10,f11,f12,f13
  f16: plane 101.3x90mm, normal (0,0,-1), area 8170.7mm2, adj f9,f10,f11,f12,f13,f14,f17,f26
  f17: plane 90x0.5mm, normal (0,-1,0), area 45mm2, adj f16,f18,f36,f43
  f18: cylinder r=6mm len=90mm, axis (1,0,0), area 848.2mm2, adj f4,f17,f34,f41
  f19: cylinder r=1mm len=90mm, axis (1,0,0), area 141.4mm2, adj f4,f20,f32,f37
  f20: plane 90x15.5mm, normal (0,1,0), area 1395mm2, adj f5,f19,f31,f35
  f21: plane 100x4.5mm, normal (0,-1,0), area 450mm2, adj f5,f6,f8,f22
  f22: cylinder r=4mm len=100mm, axis (1,0,0), area 628.3mm2, adj f6,f8,f21,f23
  f23: plane 100x58mm, normal (0,0,1), area 5800mm2, adj f6,f8,f22,f24
  f24: cylinder r=4mm len=100mm, axis (1,0,0), area 627.7mm2, adj f2,f3,f6,f8,f23,f25,f36,f38
  f25: plane 100x4.5mm, normal (0,1,0), area 450mm2, adj f2,f3,f15,f24
  f26: cylinder r=2.5mm len=10mm, axis (0,0,1), area 157.1mm2, adj f15,f16
  f27: cylinder r=3.5mm len=10mm, axis (0,0,1), area 219.9mm2, adj f15,f16
  f28: cylinder r=3.5mm len=10mm, axis (0,0,1), area 219.9mm2, adj f15,f16
  f29: cylinder r=35mm len=35mm, axis (0,0,-1), area 274.9mm2, adj f3,f7,f15,f44
  f30: cylinder r=35mm len=35mm, axis (0,0,-1), area 274.9mm2, adj f2,f7,f15,f40
  f31: cylinder r=5mm len=15.5mm, axis (0,0,-1), area 110.3mm2, adj f5,f8,f20,f32
  f32: bspline ~5.78x5mm, area 8.5mm2, adj f19,f31,f33
  f33: cylinder r=5mm len=77mm, axis (0,-1,0), area 593.3mm2, adj f4,f8,f32,f34
  f34: torus R=1mm, axis (-1,0,0), area 51.6mm2, adj f8,f18,f33,f36
  f35: cylinder r=5mm len=15.5mm, axis (0,0,-1), area 110.3mm2, adj f5,f6,f20,f37
  f36: cylinder r=5mm len=5mm, axis (0,0,1), area 15.8mm2, adj f8,f17,f24,f34,f38
  f37: bspline ~5.2x5mm, area 8.5mm2, adj f19,f35,f39
  f38: cylinder r=5mm len=74.82mm, axis (0,1,0), area 572.7mm2, adj f2,f16,f24,f36,f40
  f39: cylinder r=5mm len=77mm, axis (0,-1,0), area 593.3mm2, adj f4,f6,f37,f41
  f40: torus R=30mm, axis (0,0,1), area 409.4mm2, adj f16,f30,f38,f42
  f41: torus R=1mm, axis (1,0,0), area 51.6mm2, adj f6,f18,f39,f43
  f42: cylinder r=5mm len=30mm, axis (1,0,0), area 235.6mm2, adj f7,f16,f40,f44
  f43: cylinder r=5mm len=5mm, axis (0,0,1), area 15.8mm2, adj f6,f17,f24,f41,f45
  f44: torus R=30mm, axis (0,0,1), area 409.4mm2, adj f16,f29,f42,f45
  f45: cylinder r=5mm len=74.82mm, axis (0,-1,0), area 572.7mm2, adj f3,f16,f24,f43,f44
  f46: plane 7.11x7.11mm, normal (0,0,1), area 20.1mm2, adj f1,f47
  f47: cylinder r=3.56mm len=7.11mm, axis (0,0,1), area 60.3mm2, adj f5,f46
  f48: cylinder r=3.56mm len=7.11mm, axis (0,0,1), area 60.3mm2, adj f5,f49
  f49: plane 7.11x7.11mm, normal (0,0,1), area 20.1mm2, adj f0,f48
PLACE A rot(axis=(0,-1,0),0deg) t=(100.65,-171.12,298.19)mm
PLACE B rot(axis=(-1,0,0),90deg) t=(301.17,-338.97,376.77)mm
MATE fastened B.f15 <-> A.f310  axis (0,1,0) through (100.65,-196.52,328.19)mm
